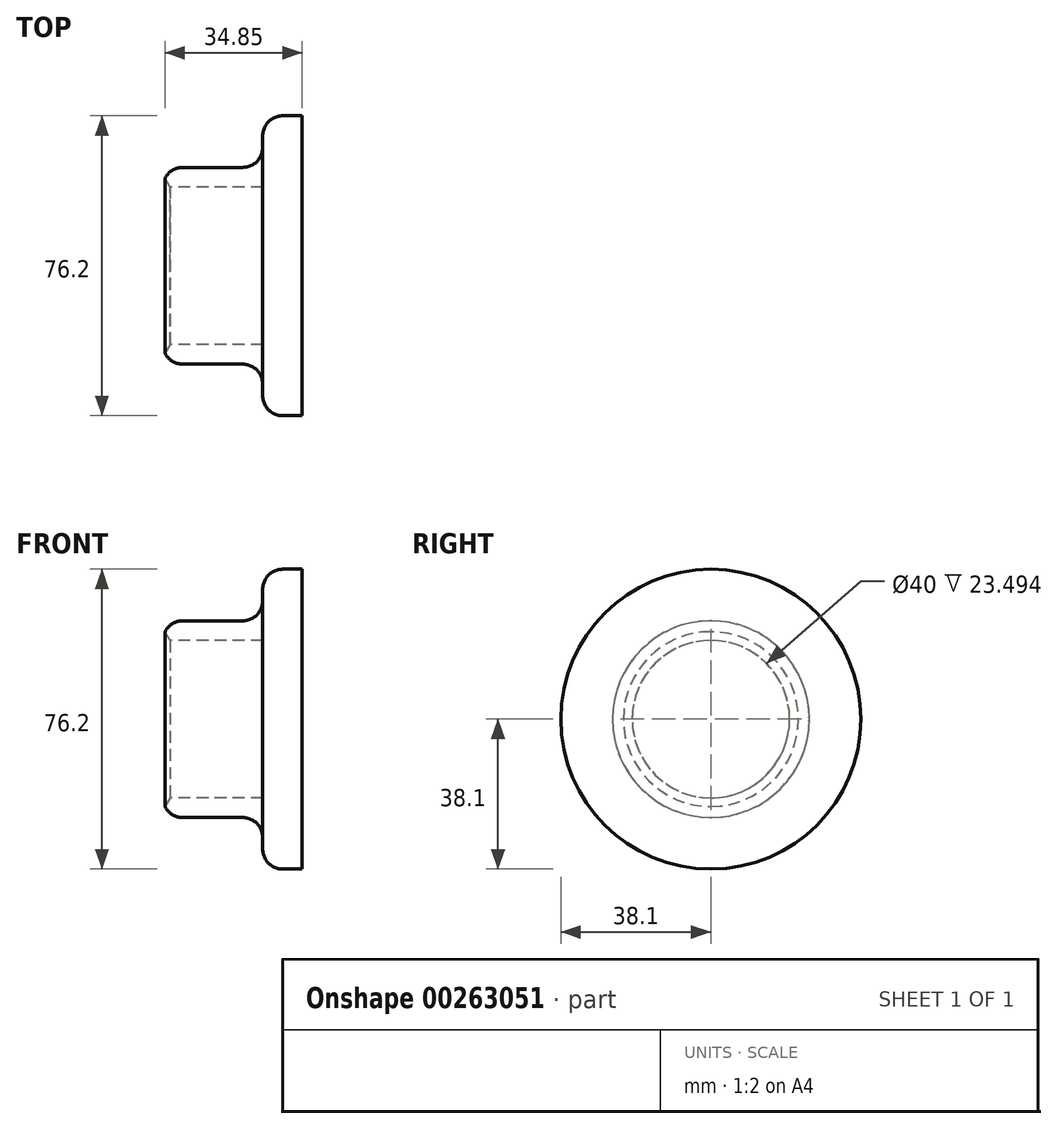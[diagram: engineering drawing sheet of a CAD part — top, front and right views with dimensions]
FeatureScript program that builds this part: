
annotation { "Feature Type Name" : "Feature", "Feature Type Description" : "" }
export const myFeature = defineFeature(function(context is Context, id is Id, definition is map)
    precondition{}
    {
        {
            var Q0;
            Q0=qCreatedBy(makeId("Right.planeOp"),FACE);
            var sketch = newSketch(context, id + "F0", { "sketchPlane" : qUnion([Q0])});
            skPoint(sketch, "E0.0", {"position": v(0, 0) * mm});
            skCircle(sketch, "E1", {"center": v(0, 0) * mm, "radius": 20 * mm});
            skCircle(sketch, "E2.0", {"center": v(0, 0) * mm, "radius": 25 * mm});
            skSolve(sketch);
        }
        {
            var Q0;
            Q0=makeQuery(id+"F0.imprint","IMPRINT",FACE,{"disambiguationData":[TD([[makeQuery(id+"F0.imprint","IMPRINT",EDGE,{"derivedFrom":sQuery(id+"F0.wireOp",EDGE,"E1")}),-1.0]])]});
            extrude(context, id + "F1", {"entities" : qUnion([Q0]), "depth" : 25.4 * mm});
        }
        {
            var Q0;
            Q0=makeQuery(id+"F1.opExtrude","CAP_FACE",FACE,{"disambiguationData":[OSD([sQuery(id+"F0.wireOp",EDGE,"E1"),sQuery(id+"F0.wireOp",EDGE,"E2.0")])],"isStart":false});
            var sketch = newSketch(context, id + "F2", { "sketchPlane" : qUnion([Q0])});
            skCircle(sketch, "E3", {"center": v(0, 0) * mm, "radius": 38.1 * mm});
            skSolve(sketch);
        }
        {
            var Q0;
            Q0=makeQuery(id+"F2.imprint","IMPRINT",FACE,{"disambiguationData":[TD([[makeQuery(id+"F2.imprint","IMPRINT",EDGE,{"derivedFrom":sQuery(id+"F2.wireOp",EDGE,"E3")}),1.0]])]});
            var Q1;
            Q1=makeQuery(id+"F2.imprint","IMPRINT",FACE,{"disambiguationData":[TD([[makeQuery(id+"F2.imprint","IMPRINT",EDGE,{"derivedFrom":makeQuery(id+"F1.opExtrude","CAP_EDGE",EDGE,{"disambiguationData":[OSD([sQuery(id+"F0.wireOp",EDGE,"E1")])],"isStart":false})}),-1.0]])]});
            var Q2;
            Q2=makeQuery(id+"F2.imprint","IMPRINT",FACE,{"disambiguationData":[TD([[makeQuery(id+"F2.imprint","IMPRINT",EDGE,{"derivedFrom":makeQuery(id+"F1.opExtrude","CAP_EDGE",EDGE,{"disambiguationData":[OSD([sQuery(id+"F0.wireOp",EDGE,"E1")])],"isStart":false})}),1.0]])]});
            extrude(context, id + "F3", {"entities" : qUnion([Q0, Q1, Q2]), "operationType" : NewBodyOperationType.ADD, "depth" : 10 * mm});
        }
        {
            var Q0;
            Q0=makeQuery(id+"F1.opExtrude","CAP_EDGE",EDGE,{"disambiguationData":[OSD([sQuery(id+"F0.wireOp",EDGE,"E2.0")])],"isStart":true});
            var Q1;
            Q1=makeQuery(id+"F1.opExtrude","SWEPT_FACE",FACE,{"disambiguationData":[OSD([sQuery(id+"F0.wireOp",EDGE,"E2.0")])]});
            var Q2;
            Q2=makeQuery(id+"F3.opExtrude","CAP_EDGE",EDGE,{"disambiguationData":[OSD([sQuery(id+"F2.wireOp",EDGE,"E3")])],"isStart":true});
            fillet(context, id + "F4", {"entities" : qUnion([Q0, Q1, Q2]), "radius" : 5.08 * mm, "tangentPropagation" : true, "allowEdgeOverflow" : false});
        }
        {
            var Q0;
            Q0=makeQuery(id+"F4.opFillet","BLEND_EDGE",EDGE,{"blendedFrom":[makeQuery(id+"F1.opExtrude","CAP_EDGE",EDGE,{"disambiguationData":[OSD([sQuery(id+"F0.wireOp",EDGE,"E2.0")])],"isStart":true}),makeQuery(id+"F1.opExtrude","SWEPT_FACE",FACE,{"disambiguationData":[OSD([sQuery(id+"F0.wireOp",EDGE,"E1")])]})],"blendedInto":[makeQuery(id+"F1.opExtrude","SWEPT_FACE",FACE,{"disambiguationData":[OSD([sQuery(id+"F0.wireOp",EDGE,"E1")])]})]});
            chamfer(context, id + "F5", {"entities" : qUnion([Q0]), "width" : 1.52 * mm, "tangentPropagation" : true});
        }
    });
